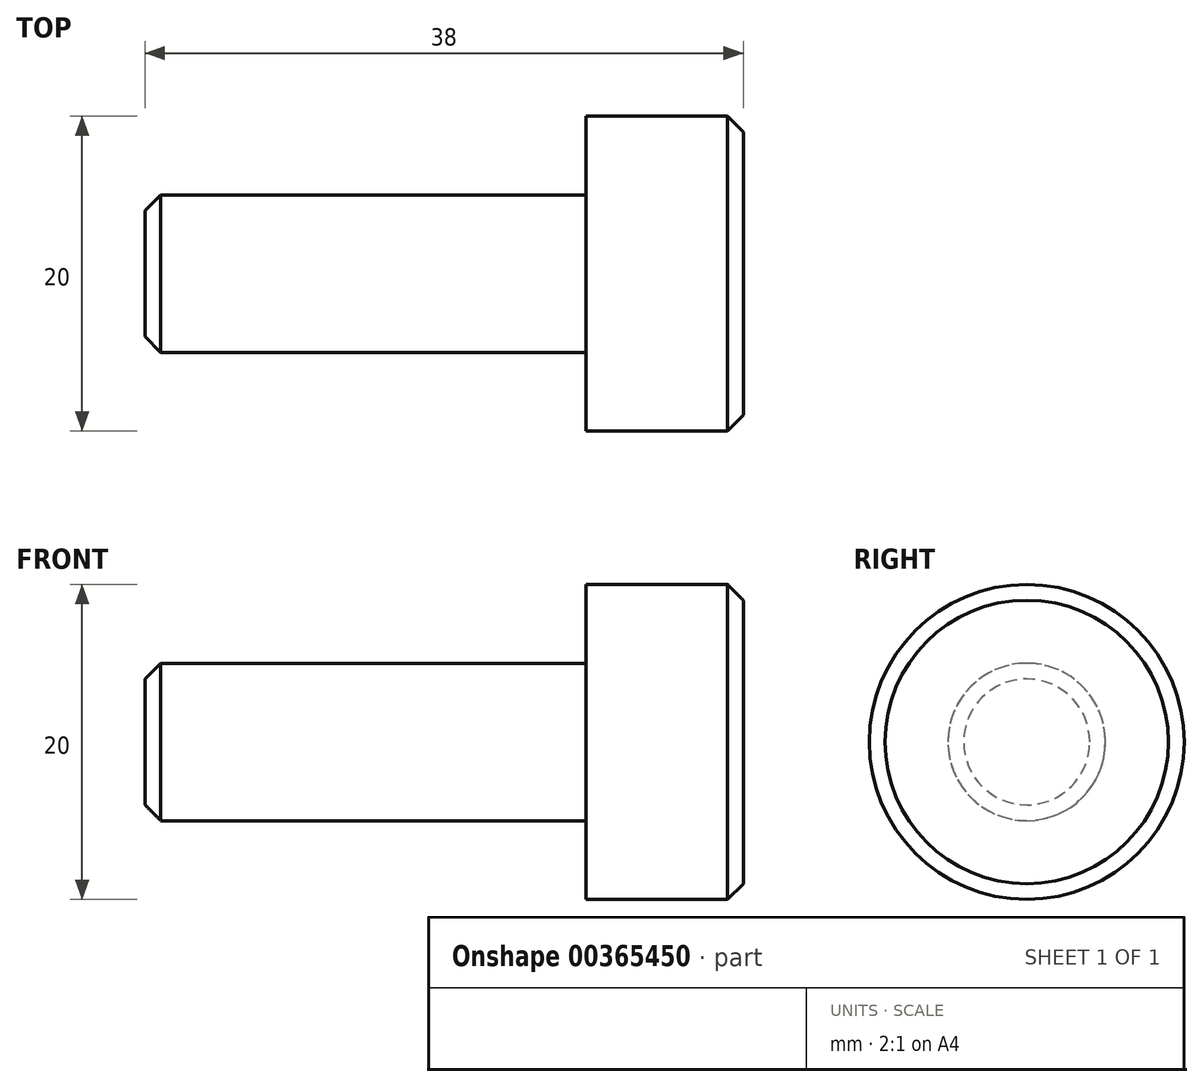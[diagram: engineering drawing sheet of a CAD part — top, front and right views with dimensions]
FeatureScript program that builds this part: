
annotation { "Feature Type Name" : "Feature", "Feature Type Description" : "" }
export const myFeature = defineFeature(function(context is Context, id is Id, definition is map)
    precondition{}
    {
        {
            var Q0;
            Q0=qCreatedBy(makeId("Front.planeOp"),FACE);
            var sketch = newSketch(context, id + "F0", { "sketchPlane" : qUnion([Q0])});
            skLineSegment(sketch, "E0", {"start": v(38, 0) * mm, "end": v(38, 10) * mm});
            skLineSegment(sketch, "E1", {"start": v(38, 10) * mm, "end": v(28, 10) * mm});
            skLineSegment(sketch, "E2", {"start": v(28, 10) * mm, "end": v(28, 5) * mm});
            skLineSegment(sketch, "E3", {"start": v(28, 5) * mm, "end": v(0, 5) * mm});
            skLineSegment(sketch, "E4", {"start": v(0, 5) * mm, "end": v(0, 0) * mm});
            skLineSegment(sketch, "E5", {"start": v(0, 0) * mm, "end": v(38, 0) * mm});
            skSolve(sketch);
        }
        {
            var Q0;
            Q0=makeQuery(id+"F0.imprint","IMPRINT",FACE,{"disambiguationData":[TD([[makeQuery(id+"F0.imprint","IMPRINT",EDGE,{"derivedFrom":sQuery(id+"F0.wireOp",EDGE,"E0")}),1.0]])]});
            var Q1;
            Q1=sQuery(id+"F0.wireOp",EDGE,"E5");
            revolve(context, id + "F1", {"entities" : qUnion([Q0]), "axis" : qUnion([Q1]), "revolveType" : RevolveType.FULL});
        }
        {
            var Q0;
            Q0=makeQuery(id+"F1.opRevolve","SWEPT_EDGE",EDGE,{"disambiguationData":[OSD([sQuery(id+"F0.wireOp",EDGE,"E0"),sQuery(id+"F0.wireOp",EDGE,"E1")])]});
            var Q1;
            Q1=makeQuery(id+"F1.opRevolve","SWEPT_EDGE",EDGE,{"disambiguationData":[OSD([sQuery(id+"F0.wireOp",EDGE,"E3"),sQuery(id+"F0.wireOp",EDGE,"E4")])]});
            chamfer(context, id + "F2", {"entities" : qUnion([Q0, Q1]), "width" : 1 * mm, "tangentPropagation" : true});
        }
    });
